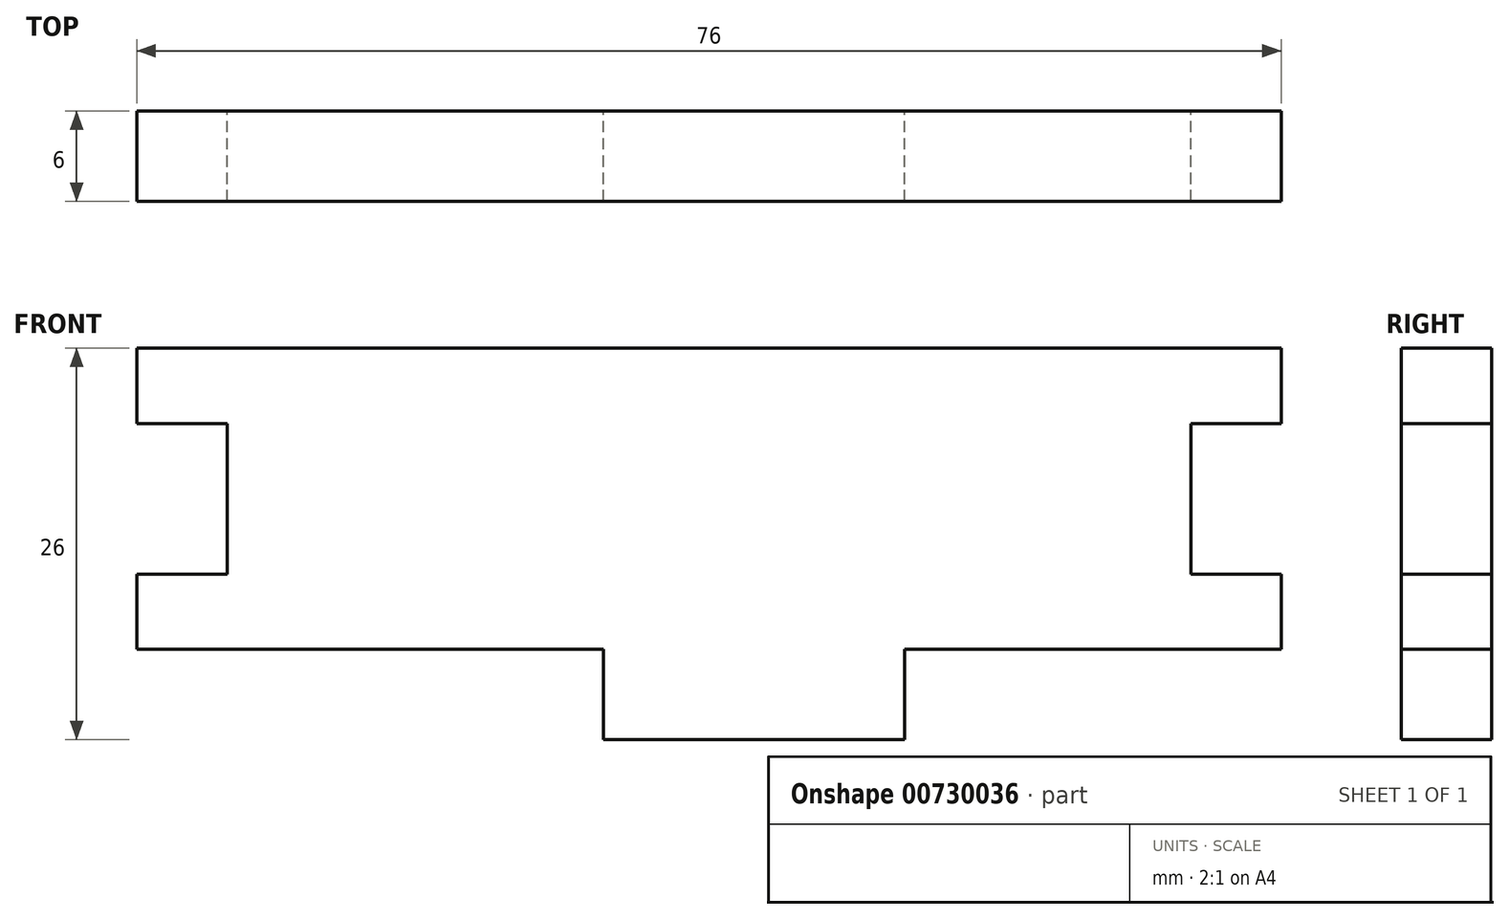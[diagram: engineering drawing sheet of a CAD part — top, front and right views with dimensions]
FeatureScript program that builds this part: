
annotation { "Feature Type Name" : "Feature", "Feature Type Description" : "" }
export const myFeature = defineFeature(function(context is Context, id is Id, definition is map)
    precondition{}
    {
        {
            var Q0;
            Q0=qCreatedBy(makeId("Front.planeOp"),FACE);
            var sketch = newSketch(context, id + "F0", { "sketchPlane" : qUnion([Q0])});
            skLineSegment(sketch, "E0.MirrorCS", {"start": v(68.7, 30.67) * mm, "end": v(62.7, 30.67) * mm});
            skLineSegment(sketch, "E1.MirrorCS", {"start": v(138.7, 35.67) * mm, "end": v(62.7, 35.67) * mm});
            skLineSegment(sketch, "E2.MirrorCS", {"start": v(138.7, 15.67) * mm, "end": v(138.7, 20.67) * mm});
            skLineSegment(sketch, "E3.MirrorCS", {"start": v(132.7, 30.67) * mm, "end": v(138.7, 30.67) * mm});
            skLineSegment(sketch, "E4.MirrorCS", {"start": v(68.7, 20.67) * mm, "end": v(68.7, 30.67) * mm});
            skLineSegment(sketch, "E5.MirrorCS", {"start": v(93.7, 9.67) * mm, "end": v(93.7, 15.67) * mm});
            skLineSegment(sketch, "E6.MirrorCS", {"start": v(62.7, 15.67) * mm, "end": v(62.7, 20.67) * mm});
            skLineSegment(sketch, "E7.MirrorCS", {"start": v(62.7, 20.67) * mm, "end": v(68.7, 20.67) * mm});
            skLineSegment(sketch, "E8.MirrorCS", {"start": v(138.7, 20.67) * mm, "end": v(132.7, 20.67) * mm});
            skLineSegment(sketch, "E9.MirrorCS", {"start": v(132.7, 20.67) * mm, "end": v(132.7, 30.67) * mm});
            skLineSegment(sketch, "E10.MirrorCS", {"start": v(138.7, 30.67) * mm, "end": v(138.7, 35.67) * mm});
            skLineSegment(sketch, "E11.MirrorCS", {"start": v(93.7, 15.67) * mm, "end": v(62.7, 15.67) * mm});
            skLineSegment(sketch, "E12.MirrorCS", {"start": v(113.7, 15.67) * mm, "end": v(113.7, 9.67) * mm});
            skLineSegment(sketch, "E13.MirrorCS", {"start": v(138.7, 15.67) * mm, "end": v(113.7, 15.67) * mm});
            skLineSegment(sketch, "E14.MirrorCS", {"start": v(62.7, 30.67) * mm, "end": v(62.7, 35.67) * mm});
            skLineSegment(sketch, "E15.MirrorCS", {"start": v(113.7, 9.67) * mm, "end": v(93.7, 9.67) * mm});
            skSolve(sketch);
        }
        {
            var Q0;
            Q0 = qSketchRegion(id + "F0", true);
            extrude(context, id + "F1", {"entities" : qUnion([Q0]), "depth" : 6 * mm, "offsetDistance" : 25 * mm});
        }
    });
